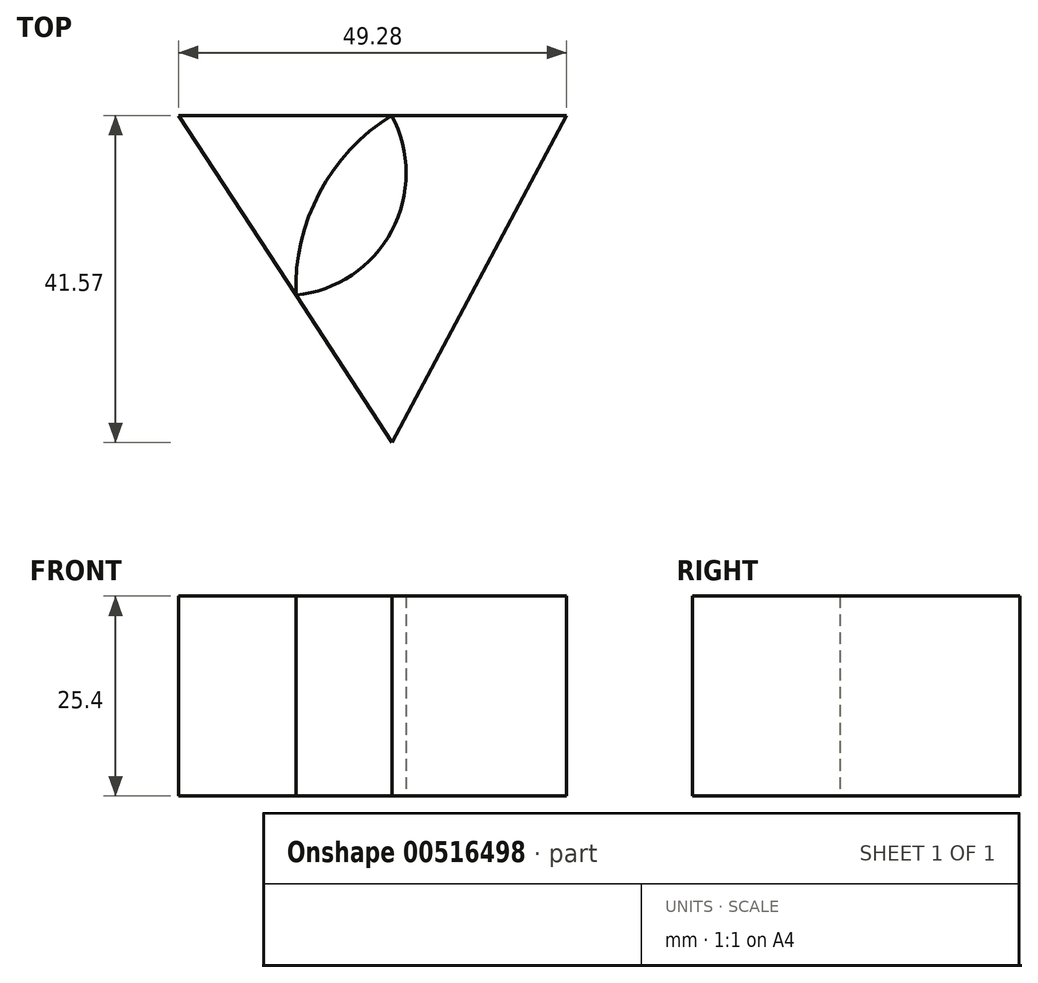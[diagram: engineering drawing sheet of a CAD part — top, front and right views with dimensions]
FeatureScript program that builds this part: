
annotation { "Feature Type Name" : "Feature", "Feature Type Description" : "" }
export const myFeature = defineFeature(function(context is Context, id is Id, definition is map)
    precondition{}
    {
        {
            var Q0;
            Q0=qCreatedBy(makeId("Top.planeOp"),FACE);
            var sketch = newSketch(context, id + "F0", { "sketchPlane" : qUnion([Q0])});
            skLineSegment(sketch, "E0", {"start": v(-22.35, 12.99) * mm, "end": v(4.78, -28.58) * mm});
            skLineSegment(sketch, "E1", {"start": v(-22.35, 12.99) * mm, "end": v(26.93, 12.99) * mm});
            skLineSegment(sketch, "E2", {"start": v(4.78, -28.58) * mm, "end": v(26.93, 12.99) * mm});
            skArc(sketch, "E3", {"start": v(4.72, 12.99) * mm, "mid": v(-4.43, 3.2) * mm, "end": v(-7.44, -9.86) * mm});
            skArc(sketch, "E4", {"start": v(-7.44, -9.86) * mm, "mid": v(4.73, -1.68) * mm, "end": v(4.72, 12.99) * mm});
            skPoint(sketch, "E5", {"position": v(0, 0) * mm});
            skSolve(sketch);
        }
        {
            var Q0;
            {var subQ4=sQuery(id+"F0.wireOp",EDGE,"E3");Q0=makeQuery(id+"F0.imprint","IMPRINT",FACE,{"disambiguationData":[TD([[makeQuery(id+"F0.imprint","IMPRINT",EDGE,{"derivedFrom":subQ4}),-1.0]])]});}
            var Q1;
            {var subQ0=sQuery(id+"F0.wireOp",EDGE,"E2");Q1=makeQuery(id+"F0.imprint","IMPRINT",FACE,{"disambiguationData":[TD([[makeQuery(id+"F0.imprint","IMPRINT",EDGE,{"derivedFrom":subQ0}),1.0]])]});}
            extrude(context, id + "F1", {"entities" : qUnion([Q0, Q1]), "depth" : 25.4 * mm, "offsetDistance" : 25.4 * mm});
        }
    });
